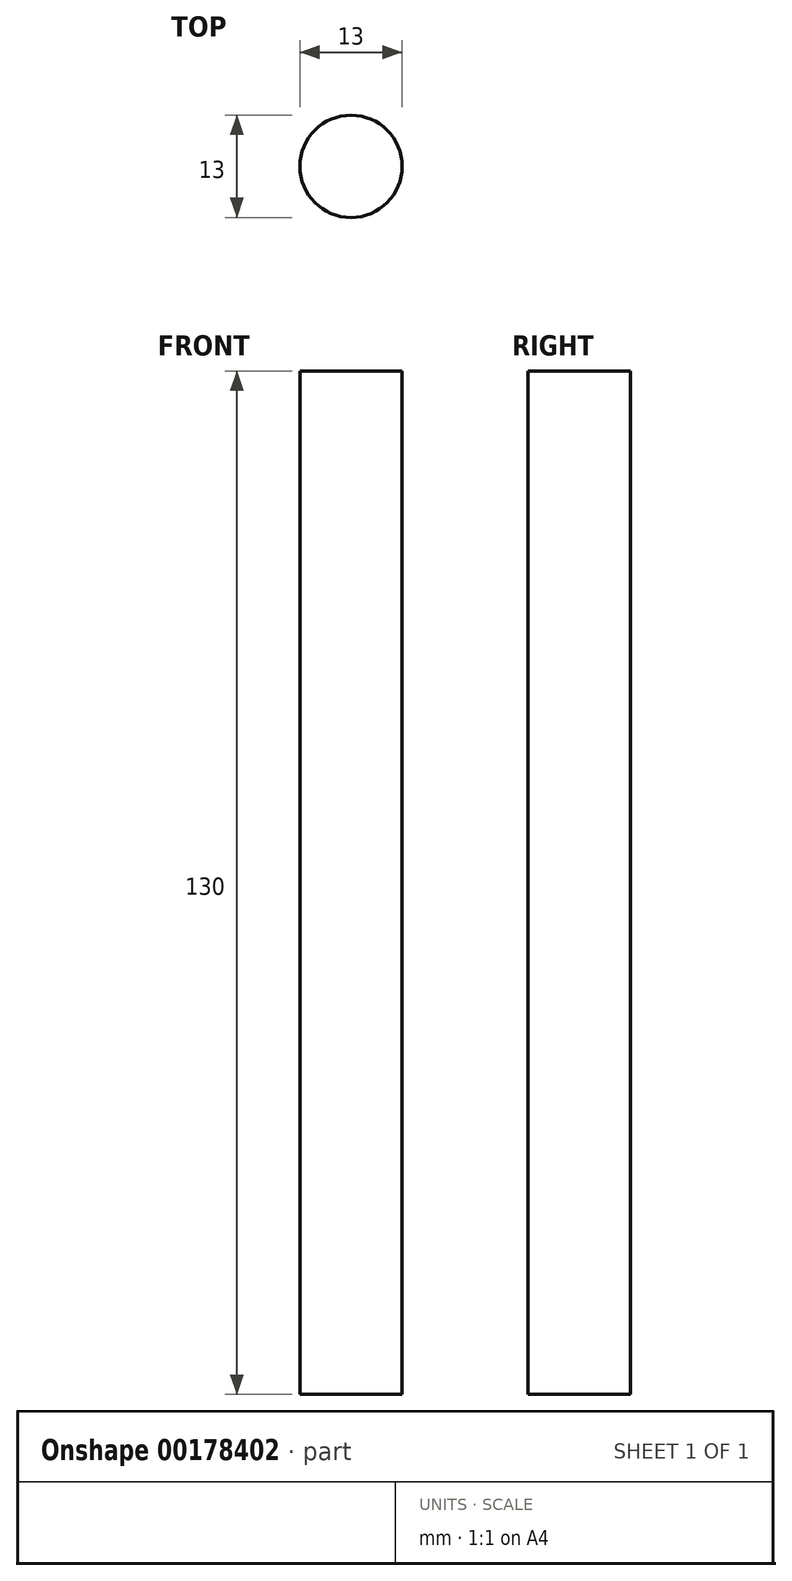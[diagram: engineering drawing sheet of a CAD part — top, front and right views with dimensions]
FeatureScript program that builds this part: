
annotation { "Feature Type Name" : "Feature", "Feature Type Description" : "" }
export const myFeature = defineFeature(function(context is Context, id is Id, definition is map)
    precondition{}
    {
        {
            var Q0;
            Q0=qCreatedBy(makeId("Top.planeOp"),FACE);
            var sketch = newSketch(context, id + "F0", { "sketchPlane" : qUnion([Q0])});
            skCircle(sketch, "E0", {"center": v(0, 0) * mm, "radius": 6.5 * mm});
            skSolve(sketch);
        }
        {
            var Q0;
            Q0 = qSketchRegion(id + "F0", true);
            extrude(context, id + "F1", {"entities" : qUnion([Q0]), "depth" : 130 * mm});
        }
    });
